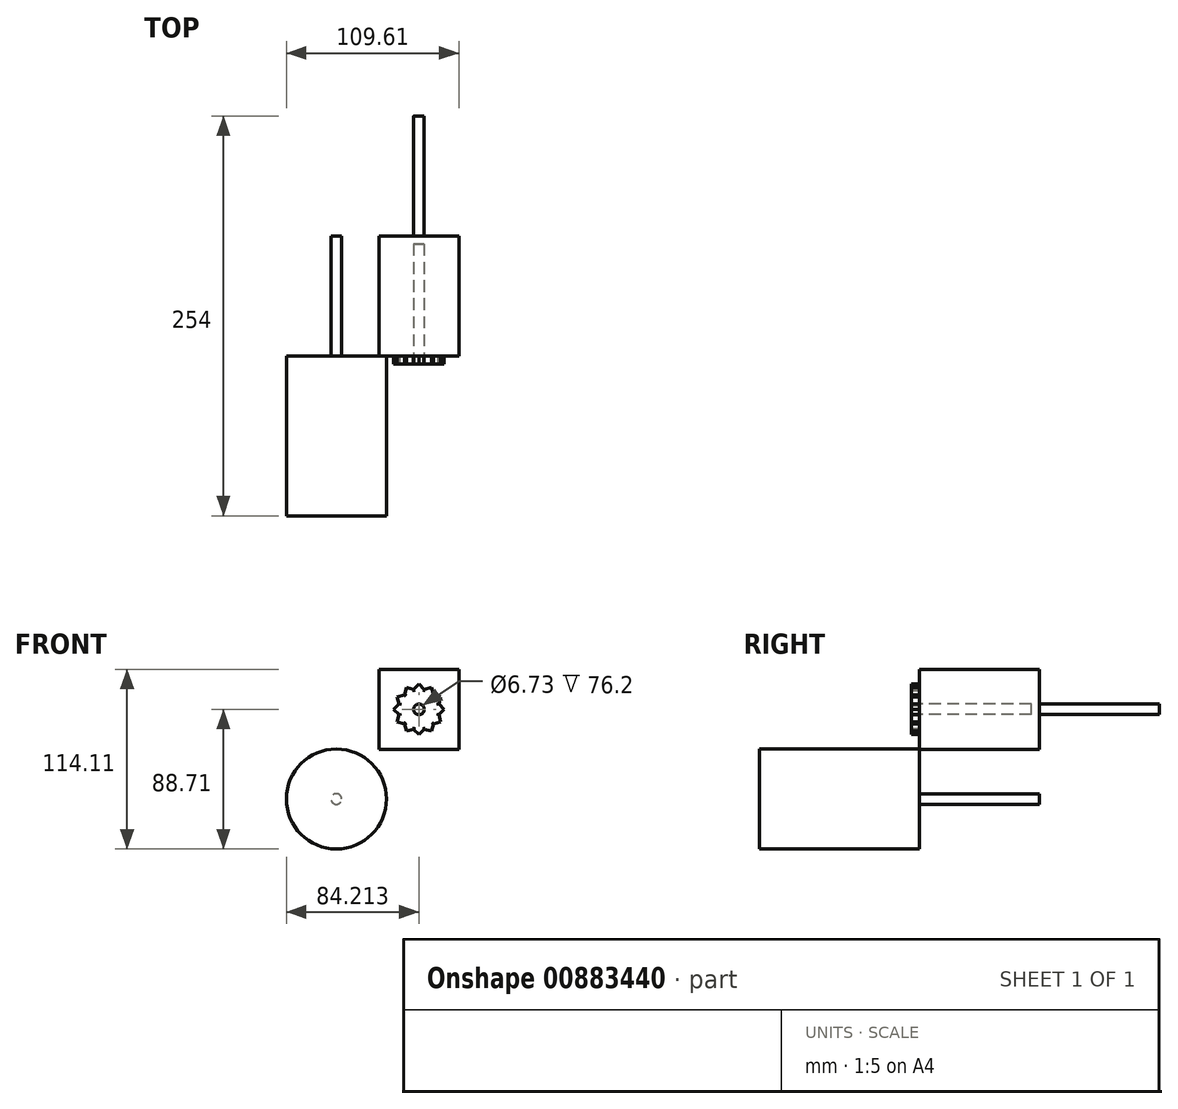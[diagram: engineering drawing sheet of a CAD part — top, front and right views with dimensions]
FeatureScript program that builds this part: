
annotation { "Feature Type Name" : "Feature", "Feature Type Description" : "" }
export const myFeature = defineFeature(function(context is Context, id is Id, definition is map)
    precondition{}
    {
        {
            var Q0;
            Q0=qCreatedBy(makeId("Front.planeOp"),FACE);
            var sketch = newSketch(context, id + "F0", { "sketchPlane" : qUnion([Q0])});
            skCircle(sketch, "E0", {"center": v(0, 0) * mm, "radius": 3.35 * mm});
            skSolve(sketch);
        }
        {
            var Q0;
            Q0 = qSketchRegion(id + "F0", true);
            extrude(context, id + "F1", {"entities" : qUnion([Q0]), "depth" : 76.2 * mm, "offsetDistance" : 25.4 * mm});
        }
        {
            var Q0;
            Q0=makeQuery(id+"F1.opExtrude","CAP_FACE",FACE,{"disambiguationData":[OSD([sQuery(id+"F0.wireOp",EDGE,"E0")])],"isStart":false});
            var sketch = newSketch(context, id + "F2", { "sketchPlane" : qUnion([Q0])});
            skCircle(sketch, "E1", {"center": v(0, 0) * mm, "radius": 31.75 * mm});
            skSolve(sketch);
        }
        {
            var Q0;
            Q0 = qSketchRegion(id + "F2", true);
            extrude(context, id + "F3", {"entities" : qUnion([Q0]), "operationType" : NewBodyOperationType.ADD, "depth" : 101.6 * mm, "offsetDistance" : 25.4 * mm});
        }
        {
            var Q0;
            Q0=qCreatedBy(makeId("Front.planeOp"),FACE);
            var sketch = newSketch(context, id + "F4", { "sketchPlane" : qUnion([Q0])});
            skLineSegment(sketch, "E2.bottom", {"start": v(27.06, 82.36) * mm, "end": v(77.86, 82.36) * mm});
            skLineSegment(sketch, "E2.top", {"start": v(27.06, 31.56) * mm, "end": v(77.86, 31.56) * mm});
            skLineSegment(sketch, "E2.left", {"start": v(27.06, 82.36) * mm, "end": v(27.06, 31.56) * mm});
            skLineSegment(sketch, "E2.right", {"start": v(77.86, 82.36) * mm, "end": v(77.86, 31.56) * mm});
            skSolve(sketch);
        }
        {
            var Q0;
            Q0 = qSketchRegion(id + "F4", true);
            extrude(context, id + "F5", {"entities" : qUnion([Q0]), "depth" : 76.2 * mm, "offsetDistance" : 25.4 * mm});
        }
        {
            var Q0;
            Q0=makeQuery(id+"F5.opExtrude","CAP_FACE",FACE,{"disambiguationData":[OSD([sQuery(id+"F4.wireOp",EDGE,"E2.bottom"),sQuery(id+"F4.wireOp",EDGE,"E2.top"),sQuery(id+"F4.wireOp",EDGE,"E2.left"),sQuery(id+"F4.wireOp",EDGE,"E2.right")])],"isStart":true});
            var sketch = newSketch(context, id + "F6", { "sketchPlane" : qUnion([Q0])});
            skCircle(sketch, "E3", {"center": v(-52.46, 56.96) * mm, "radius": 3.35 * mm});
            skSolve(sketch);
        }
        {
            var Q0;
            Q0 = qSketchRegion(id + "F6", true);
            extrude(context, id + "F7", {"entities" : qUnion([Q0]), "operationType" : NewBodyOperationType.ADD, "depth" : 76.2 * mm, "offsetDistance" : 25.4 * mm});
        }
        {
            var Q0;
            Q0=makeQuery(id+"F5.opExtrude","CAP_FACE",FACE,{"disambiguationData":[OSD([sQuery(id+"F4.wireOp",EDGE,"E2.bottom"),sQuery(id+"F4.wireOp",EDGE,"E2.top"),sQuery(id+"F4.wireOp",EDGE,"E2.left"),sQuery(id+"F4.wireOp",EDGE,"E2.right")])],"isStart":false});
            var sketch = newSketch(context, id + "F8", { "sketchPlane" : qUnion([Q0])});
            skCircle(sketch, "E4", {"center": v(52.46, 56.96) * mm, "radius": 12.7 * mm});
            skLineSegment(sketch, "E5", {"start": v(48.51, 69.03) * mm, "end": v(52.46, 72.98) * mm});
            skLineSegment(sketch, "E6", {"start": v(56.41, 69.03) * mm, "end": v(52.46, 72.98) * mm});
            skLineSegment(sketch, "E7", {"start": v(48.51, 69.03) * mm, "end": v(56.41, 69.03) * mm});
            skLineSegment(sketch, "E8.1.0", {"start": v(49.85, 69.39) * mm, "end": v(44.45, 70.83) * mm});
            skLineSegment(sketch, "E8.1.1", {"start": v(43, 65.44) * mm, "end": v(44.45, 70.83) * mm});
            skLineSegment(sketch, "E8.1.2", {"start": v(43, 65.44) * mm, "end": v(49.85, 69.39) * mm});
            skLineSegment(sketch, "E8.2.0", {"start": v(43.99, 66.42) * mm, "end": v(38.59, 64.97) * mm});
            skLineSegment(sketch, "E8.2.1", {"start": v(40.03, 59.57) * mm, "end": v(38.59, 64.97) * mm});
            skLineSegment(sketch, "E8.2.2", {"start": v(40.03, 59.57) * mm, "end": v(43.99, 66.42) * mm});
            skLineSegment(sketch, "E8.3.0", {"start": v(40.4, 60.91) * mm, "end": v(36.44, 56.96) * mm});
            skLineSegment(sketch, "E8.3.1", {"start": v(40.4, 53) * mm, "end": v(36.44, 56.96) * mm});
            skLineSegment(sketch, "E8.3.2", {"start": v(40.4, 53) * mm, "end": v(40.4, 60.91) * mm});
            skLineSegment(sketch, "E8.4.0", {"start": v(40.03, 54.35) * mm, "end": v(38.59, 48.95) * mm});
            skLineSegment(sketch, "E8.4.1", {"start": v(43.99, 47.5) * mm, "end": v(38.59, 48.95) * mm});
            skLineSegment(sketch, "E8.4.2", {"start": v(43.99, 47.5) * mm, "end": v(40.03, 54.35) * mm});
            skLineSegment(sketch, "E8.5.0", {"start": v(43, 48.48) * mm, "end": v(44.45, 43.09) * mm});
            skLineSegment(sketch, "E8.5.1", {"start": v(49.85, 44.53) * mm, "end": v(44.45, 43.09) * mm});
            skLineSegment(sketch, "E8.5.2", {"start": v(49.85, 44.53) * mm, "end": v(43, 48.48) * mm});
            skLineSegment(sketch, "E8.6.0", {"start": v(48.51, 44.89) * mm, "end": v(52.46, 40.94) * mm});
            skLineSegment(sketch, "E8.6.1", {"start": v(56.41, 44.89) * mm, "end": v(52.46, 40.94) * mm});
            skLineSegment(sketch, "E8.6.2", {"start": v(56.41, 44.89) * mm, "end": v(48.51, 44.89) * mm});
            skLineSegment(sketch, "E8.7.0", {"start": v(55.08, 44.53) * mm, "end": v(60.47, 43.09) * mm});
            skLineSegment(sketch, "E8.7.1", {"start": v(61.92, 48.48) * mm, "end": v(60.47, 43.09) * mm});
            skLineSegment(sketch, "E8.7.2", {"start": v(61.92, 48.48) * mm, "end": v(55.08, 44.53) * mm});
            skLineSegment(sketch, "E8.8.0", {"start": v(60.94, 47.5) * mm, "end": v(66.34, 48.95) * mm});
            skLineSegment(sketch, "E8.8.1", {"start": v(64.9, 54.35) * mm, "end": v(66.34, 48.95) * mm});
            skLineSegment(sketch, "E8.8.2", {"start": v(64.9, 54.35) * mm, "end": v(60.94, 47.5) * mm});
            skLineSegment(sketch, "E8.9.0", {"start": v(64.53, 53) * mm, "end": v(68.48, 56.96) * mm});
            skLineSegment(sketch, "E8.9.1", {"start": v(64.53, 60.91) * mm, "end": v(68.48, 56.96) * mm});
            skLineSegment(sketch, "E8.9.2", {"start": v(64.53, 60.91) * mm, "end": v(64.53, 53) * mm});
            skLineSegment(sketch, "E8.10.0", {"start": v(64.9, 59.57) * mm, "end": v(66.34, 64.97) * mm});
            skLineSegment(sketch, "E8.10.1", {"start": v(60.94, 66.42) * mm, "end": v(66.34, 64.97) * mm});
            skLineSegment(sketch, "E8.10.2", {"start": v(60.94, 66.42) * mm, "end": v(64.9, 59.57) * mm});
            skLineSegment(sketch, "E8.11.0", {"start": v(61.92, 65.44) * mm, "end": v(60.47, 70.83) * mm});
            skLineSegment(sketch, "E8.11.1", {"start": v(55.08, 69.39) * mm, "end": v(60.47, 70.83) * mm});
            skLineSegment(sketch, "E8.11.2", {"start": v(55.08, 69.39) * mm, "end": v(61.92, 65.44) * mm});
            skSolve(sketch);
        }
        {
            var Q0;
            {var subQ0=sQuery(id+"F8.wireOp",EDGE,"E8.9.1");var subQ3=sQuery(id+"F8.wireOp",EDGE,"E8.10.0");var subQ5=makeQuery(id+"F8.imprint","INTERSECT",VERTEX,{"derivedFrom":[subQ0,subQ3]});Q0=makeQuery(id+"F8.imprint","IMPRINT",FACE,{"disambiguationData":[TD([[makeQuery(id+"F8.imprint","IMPRINT",EDGE,{"disambiguationData":[TD([[subQ5,1.0]])],"derivedFrom":subQ0}),-1.0]])]});}
            var Q1;
            {var subQ0=sQuery(id+"F8.wireOp",EDGE,"E8.10.1");var subQ3=sQuery(id+"F8.wireOp",EDGE,"E8.11.0");var subQ5=makeQuery(id+"F8.imprint","INTERSECT",VERTEX,{"derivedFrom":[subQ0,subQ3]});Q1=makeQuery(id+"F8.imprint","IMPRINT",FACE,{"disambiguationData":[TD([[makeQuery(id+"F8.imprint","IMPRINT",EDGE,{"disambiguationData":[TD([[subQ5,1.0]])],"derivedFrom":subQ0}),-1.0]])]});}
            var Q2;
            {var subQ0=sQuery(id+"F8.wireOp",EDGE,"E6");var subQ3=sQuery(id+"F8.wireOp",EDGE,"E8.11.1");var subQ5=makeQuery(id+"F8.imprint","INTERSECT",VERTEX,{"derivedFrom":[subQ0,subQ3]});Q2=makeQuery(id+"F8.imprint","IMPRINT",FACE,{"disambiguationData":[TD([[makeQuery(id+"F8.imprint","IMPRINT",EDGE,{"disambiguationData":[TD([[subQ5,1.0]])],"derivedFrom":subQ0}),1.0]])]});}
            var Q3;
            {var subQ0=sQuery(id+"F8.wireOp",EDGE,"E5");var subQ3=sQuery(id+"F8.wireOp",EDGE,"E8.1.0");var subQ5=makeQuery(id+"F8.imprint","INTERSECT",VERTEX,{"derivedFrom":[subQ0,subQ3]});Q3=makeQuery(id+"F8.imprint","IMPRINT",FACE,{"disambiguationData":[TD([[makeQuery(id+"F8.imprint","IMPRINT",EDGE,{"disambiguationData":[TD([[subQ5,1.0]])],"derivedFrom":subQ0}),-1.0]])]});}
            var Q4;
            {var subQ0=sQuery(id+"F8.wireOp",EDGE,"E8.1.1");var subQ3=sQuery(id+"F8.wireOp",EDGE,"E8.2.0");var subQ5=makeQuery(id+"F8.imprint","INTERSECT",VERTEX,{"derivedFrom":[subQ0,subQ3]});Q4=makeQuery(id+"F8.imprint","IMPRINT",FACE,{"disambiguationData":[TD([[makeQuery(id+"F8.imprint","IMPRINT",EDGE,{"disambiguationData":[TD([[subQ5,1.0]])],"derivedFrom":subQ0}),-1.0]])]});}
            var Q5;
            {var subQ0=sQuery(id+"F8.wireOp",EDGE,"E8.2.1");var subQ3=sQuery(id+"F8.wireOp",EDGE,"E8.3.0");var subQ5=makeQuery(id+"F8.imprint","INTERSECT",VERTEX,{"derivedFrom":[subQ0,subQ3]});Q5=makeQuery(id+"F8.imprint","IMPRINT",FACE,{"disambiguationData":[TD([[makeQuery(id+"F8.imprint","IMPRINT",EDGE,{"disambiguationData":[TD([[subQ5,1.0]])],"derivedFrom":subQ0}),-1.0]])]});}
            var Q6;
            {var subQ0=sQuery(id+"F8.wireOp",EDGE,"E8.3.1");var subQ3=sQuery(id+"F8.wireOp",EDGE,"E8.4.0");var subQ5=makeQuery(id+"F8.imprint","INTERSECT",VERTEX,{"derivedFrom":[subQ0,subQ3]});Q6=makeQuery(id+"F8.imprint","IMPRINT",FACE,{"disambiguationData":[TD([[makeQuery(id+"F8.imprint","IMPRINT",EDGE,{"disambiguationData":[TD([[subQ5,1.0]])],"derivedFrom":subQ0}),-1.0]])]});}
            var Q7;
            {var subQ0=sQuery(id+"F8.wireOp",EDGE,"E8.4.1");var subQ3=sQuery(id+"F8.wireOp",EDGE,"E8.5.0");var subQ5=makeQuery(id+"F8.imprint","INTERSECT",VERTEX,{"derivedFrom":[subQ0,subQ3]});Q7=makeQuery(id+"F8.imprint","IMPRINT",FACE,{"disambiguationData":[TD([[makeQuery(id+"F8.imprint","IMPRINT",EDGE,{"disambiguationData":[TD([[subQ5,1.0]])],"derivedFrom":subQ0}),-1.0]])]});}
            var Q8;
            {var subQ0=sQuery(id+"F8.wireOp",EDGE,"E8.5.1");var subQ3=sQuery(id+"F8.wireOp",EDGE,"E8.6.0");var subQ5=makeQuery(id+"F8.imprint","INTERSECT",VERTEX,{"derivedFrom":[subQ0,subQ3]});Q8=makeQuery(id+"F8.imprint","IMPRINT",FACE,{"disambiguationData":[TD([[makeQuery(id+"F8.imprint","IMPRINT",EDGE,{"disambiguationData":[TD([[subQ5,1.0]])],"derivedFrom":subQ0}),-1.0]])]});}
            var Q9;
            {var subQ0=sQuery(id+"F8.wireOp",EDGE,"E8.6.1");var subQ3=sQuery(id+"F8.wireOp",EDGE,"E8.7.0");var subQ5=makeQuery(id+"F8.imprint","INTERSECT",VERTEX,{"derivedFrom":[subQ0,subQ3]});Q9=makeQuery(id+"F8.imprint","IMPRINT",FACE,{"disambiguationData":[TD([[makeQuery(id+"F8.imprint","IMPRINT",EDGE,{"disambiguationData":[TD([[subQ5,1.0]])],"derivedFrom":subQ0}),-1.0]])]});}
            var Q10;
            {var subQ0=sQuery(id+"F8.wireOp",EDGE,"E8.7.1");var subQ3=sQuery(id+"F8.wireOp",EDGE,"E8.8.0");var subQ5=makeQuery(id+"F8.imprint","INTERSECT",VERTEX,{"derivedFrom":[subQ0,subQ3]});Q10=makeQuery(id+"F8.imprint","IMPRINT",FACE,{"disambiguationData":[TD([[makeQuery(id+"F8.imprint","IMPRINT",EDGE,{"disambiguationData":[TD([[subQ5,1.0]])],"derivedFrom":subQ0}),-1.0]])]});}
            var Q11;
            {var subQ0=sQuery(id+"F8.wireOp",EDGE,"E8.8.1");var subQ3=sQuery(id+"F8.wireOp",EDGE,"E8.9.0");var subQ5=makeQuery(id+"F8.imprint","INTERSECT",VERTEX,{"derivedFrom":[subQ0,subQ3]});Q11=makeQuery(id+"F8.imprint","IMPRINT",FACE,{"disambiguationData":[TD([[makeQuery(id+"F8.imprint","IMPRINT",EDGE,{"disambiguationData":[TD([[subQ5,1.0]])],"derivedFrom":subQ0}),-1.0]])]});}
            var Q12;
            {var subQ0=sQuery(id+"F8.wireOp",EDGE,"E8.10.1");var subQ1=sQuery(id+"F8.wireOp",EDGE,"E8.10.0");var subQ2=makeQuery(id+"F8.imprint","INTERSECT",VERTEX,{"derivedFrom":[subQ1,subQ0]});Q12=makeQuery(id+"F8.imprint","IMPRINT",FACE,{"disambiguationData":[TD([[makeQuery(id+"F8.imprint","IMPRINT",EDGE,{"disambiguationData":[TD([[subQ2,1.0]])],"derivedFrom":subQ1}),1.0]])]});}
            var Q13;
            {var subQ0=sQuery(id+"F8.wireOp",EDGE,"E8.11.1");var subQ1=sQuery(id+"F8.wireOp",EDGE,"E8.11.0");var subQ2=makeQuery(id+"F8.imprint","INTERSECT",VERTEX,{"derivedFrom":[subQ1,subQ0]});Q13=makeQuery(id+"F8.imprint","IMPRINT",FACE,{"disambiguationData":[TD([[makeQuery(id+"F8.imprint","IMPRINT",EDGE,{"disambiguationData":[TD([[subQ2,1.0]])],"derivedFrom":subQ1}),1.0]])]});}
            var Q14;
            {var subQ3=sQuery(id+"F8.wireOp",EDGE,"E5");var subQ5=sQuery(id+"F8.wireOp",EDGE,"E6");var subQ6=makeQuery(id+"F8.imprint","INTERSECT",VERTEX,{"derivedFrom":[subQ3,subQ5]});Q14=makeQuery(id+"F8.imprint","IMPRINT",FACE,{"disambiguationData":[TD([[makeQuery(id+"F8.imprint","IMPRINT",EDGE,{"disambiguationData":[TD([[subQ6,1.0]])],"derivedFrom":subQ3}),-1.0]])]});}
            var Q15;
            {var subQ0=sQuery(id+"F8.wireOp",EDGE,"E8.2.1");var subQ1=sQuery(id+"F8.wireOp",EDGE,"E8.2.0");var subQ2=makeQuery(id+"F8.imprint","INTERSECT",VERTEX,{"derivedFrom":[subQ1,subQ0]});Q15=makeQuery(id+"F8.imprint","IMPRINT",FACE,{"disambiguationData":[TD([[makeQuery(id+"F8.imprint","IMPRINT",EDGE,{"disambiguationData":[TD([[subQ2,1.0]])],"derivedFrom":subQ1}),1.0]])]});}
            var Q16;
            {var subQ0=sQuery(id+"F8.wireOp",EDGE,"E8.3.1");var subQ1=sQuery(id+"F8.wireOp",EDGE,"E8.3.0");var subQ2=makeQuery(id+"F8.imprint","INTERSECT",VERTEX,{"derivedFrom":[subQ1,subQ0]});Q16=makeQuery(id+"F8.imprint","IMPRINT",FACE,{"disambiguationData":[TD([[makeQuery(id+"F8.imprint","IMPRINT",EDGE,{"disambiguationData":[TD([[subQ2,1.0]])],"derivedFrom":subQ1}),1.0]])]});}
            var Q17;
            {var subQ0=sQuery(id+"F8.wireOp",EDGE,"E8.4.1");var subQ1=sQuery(id+"F8.wireOp",EDGE,"E8.4.0");var subQ2=makeQuery(id+"F8.imprint","INTERSECT",VERTEX,{"derivedFrom":[subQ1,subQ0]});Q17=makeQuery(id+"F8.imprint","IMPRINT",FACE,{"disambiguationData":[TD([[makeQuery(id+"F8.imprint","IMPRINT",EDGE,{"disambiguationData":[TD([[subQ2,1.0]])],"derivedFrom":subQ1}),1.0]])]});}
            var Q18;
            {var subQ0=sQuery(id+"F8.wireOp",EDGE,"E8.5.1");var subQ1=sQuery(id+"F8.wireOp",EDGE,"E8.5.0");var subQ2=makeQuery(id+"F8.imprint","INTERSECT",VERTEX,{"derivedFrom":[subQ1,subQ0]});Q18=makeQuery(id+"F8.imprint","IMPRINT",FACE,{"disambiguationData":[TD([[makeQuery(id+"F8.imprint","IMPRINT",EDGE,{"disambiguationData":[TD([[subQ2,1.0]])],"derivedFrom":subQ1}),1.0]])]});}
            var Q19;
            {var subQ0=sQuery(id+"F8.wireOp",EDGE,"E8.6.1");var subQ1=sQuery(id+"F8.wireOp",EDGE,"E8.6.0");var subQ2=makeQuery(id+"F8.imprint","INTERSECT",VERTEX,{"derivedFrom":[subQ1,subQ0]});Q19=makeQuery(id+"F8.imprint","IMPRINT",FACE,{"disambiguationData":[TD([[makeQuery(id+"F8.imprint","IMPRINT",EDGE,{"disambiguationData":[TD([[subQ2,1.0]])],"derivedFrom":subQ1}),1.0]])]});}
            var Q20;
            {var subQ0=sQuery(id+"F8.wireOp",EDGE,"E8.7.1");var subQ1=sQuery(id+"F8.wireOp",EDGE,"E8.7.0");var subQ2=makeQuery(id+"F8.imprint","INTERSECT",VERTEX,{"derivedFrom":[subQ1,subQ0]});Q20=makeQuery(id+"F8.imprint","IMPRINT",FACE,{"disambiguationData":[TD([[makeQuery(id+"F8.imprint","IMPRINT",EDGE,{"disambiguationData":[TD([[subQ2,1.0]])],"derivedFrom":subQ1}),1.0]])]});}
            var Q21;
            {var subQ0=sQuery(id+"F8.wireOp",EDGE,"E8.8.1");var subQ1=sQuery(id+"F8.wireOp",EDGE,"E8.8.0");var subQ2=makeQuery(id+"F8.imprint","INTERSECT",VERTEX,{"derivedFrom":[subQ1,subQ0]});Q21=makeQuery(id+"F8.imprint","IMPRINT",FACE,{"disambiguationData":[TD([[makeQuery(id+"F8.imprint","IMPRINT",EDGE,{"disambiguationData":[TD([[subQ2,1.0]])],"derivedFrom":subQ1}),1.0]])]});}
            var Q22;
            {var subQ0=sQuery(id+"F8.wireOp",EDGE,"E8.9.1");var subQ1=sQuery(id+"F8.wireOp",EDGE,"E8.9.0");var subQ2=makeQuery(id+"F8.imprint","INTERSECT",VERTEX,{"derivedFrom":[subQ1,subQ0]});Q22=makeQuery(id+"F8.imprint","IMPRINT",FACE,{"disambiguationData":[TD([[makeQuery(id+"F8.imprint","IMPRINT",EDGE,{"disambiguationData":[TD([[subQ2,1.0]])],"derivedFrom":subQ1}),1.0]])]});}
            var Q23;
            {var subQ15=sQuery(id+"F8.wireOp",EDGE,"E8.1.2");var subQ16=sQuery(id+"F8.wireOp",EDGE,"E7");var subQ17=makeQuery(id+"F8.imprint","INTERSECT",VERTEX,{"derivedFrom":[subQ16,subQ15]});Q23=makeQuery(id+"F8.imprint","IMPRINT",FACE,{"disambiguationData":[TD([[makeQuery(id+"F8.imprint","IMPRINT",EDGE,{"disambiguationData":[TD([[subQ17,-1.0]])],"derivedFrom":subQ16}),-1.0]])]});}
            var Q24;
            {var subQ0=sQuery(id+"F8.wireOp",EDGE,"E7");var subQ5=sQuery(id+"F8.wireOp",EDGE,"E8.1.2");var subQ6=makeQuery(id+"F8.imprint","INTERSECT",VERTEX,{"derivedFrom":[subQ0,subQ5]});Q24=makeQuery(id+"F8.imprint","IMPRINT",FACE,{"disambiguationData":[TD([[makeQuery(id+"F8.imprint","IMPRINT",EDGE,{"disambiguationData":[TD([[subQ6,1.0]])],"derivedFrom":subQ5}),1.0]])]});}
            var Q25;
            {var subQ0=sQuery(id+"F8.wireOp",EDGE,"E8.1.1");var subQ1=sQuery(id+"F8.wireOp",EDGE,"E8.1.0");var subQ2=makeQuery(id+"F8.imprint","INTERSECT",VERTEX,{"derivedFrom":[subQ1,subQ0]});Q25=makeQuery(id+"F8.imprint","IMPRINT",FACE,{"disambiguationData":[TD([[makeQuery(id+"F8.imprint","IMPRINT",EDGE,{"disambiguationData":[TD([[subQ2,1.0]])],"derivedFrom":subQ1}),1.0]])]});}
            var Q26;
            {var subQ0=sQuery(id+"F8.wireOp",EDGE,"E8.1.2");var subQ5=sQuery(id+"F8.wireOp",EDGE,"E7");var subQ7=makeQuery(id+"F8.imprint","INTERSECT",VERTEX,{"derivedFrom":[subQ5,subQ0]});Q26=makeQuery(id+"F8.imprint","IMPRINT",FACE,{"disambiguationData":[TD([[makeQuery(id+"F8.imprint","IMPRINT",EDGE,{"disambiguationData":[TD([[subQ7,-1.0]])],"derivedFrom":subQ5}),1.0]])]});}
            var Q27;
            {var subQ0=sQuery(id+"F8.wireOp",EDGE,"E7");var subQ5=sQuery(id+"F8.wireOp",EDGE,"E8.11.2");var subQ7=makeQuery(id+"F8.imprint","INTERSECT",VERTEX,{"derivedFrom":[subQ0,subQ5]});Q27=makeQuery(id+"F8.imprint","IMPRINT",FACE,{"disambiguationData":[TD([[makeQuery(id+"F8.imprint","IMPRINT",EDGE,{"disambiguationData":[TD([[subQ7,-1.0]])],"derivedFrom":subQ5}),1.0]])]});}
            var Q28;
            {var subQ0=sQuery(id+"F8.wireOp",EDGE,"E8.9.2");var subQ5=sQuery(id+"F8.wireOp",EDGE,"E8.10.2");var subQ6=makeQuery(id+"F8.imprint","INTERSECT",VERTEX,{"derivedFrom":[subQ0,subQ5]});Q28=makeQuery(id+"F8.imprint","IMPRINT",FACE,{"disambiguationData":[TD([[makeQuery(id+"F8.imprint","IMPRINT",EDGE,{"disambiguationData":[TD([[subQ6,1.0]])],"derivedFrom":subQ5}),1.0]])]});}
            var Q29;
            {var subQ0=sQuery(id+"F8.wireOp",EDGE,"E8.8.2");var subQ5=sQuery(id+"F8.wireOp",EDGE,"E8.9.2");var subQ6=makeQuery(id+"F8.imprint","INTERSECT",VERTEX,{"derivedFrom":[subQ0,subQ5]});Q29=makeQuery(id+"F8.imprint","IMPRINT",FACE,{"disambiguationData":[TD([[makeQuery(id+"F8.imprint","IMPRINT",EDGE,{"disambiguationData":[TD([[subQ6,1.0]])],"derivedFrom":subQ5}),1.0]])]});}
            var Q30;
            {var subQ0=sQuery(id+"F8.wireOp",EDGE,"E8.7.2");var subQ5=sQuery(id+"F8.wireOp",EDGE,"E8.8.2");var subQ6=makeQuery(id+"F8.imprint","INTERSECT",VERTEX,{"derivedFrom":[subQ0,subQ5]});Q30=makeQuery(id+"F8.imprint","IMPRINT",FACE,{"disambiguationData":[TD([[makeQuery(id+"F8.imprint","IMPRINT",EDGE,{"disambiguationData":[TD([[subQ6,1.0]])],"derivedFrom":subQ5}),1.0]])]});}
            var Q31;
            {var subQ0=sQuery(id+"F8.wireOp",EDGE,"E8.6.2");var subQ5=sQuery(id+"F8.wireOp",EDGE,"E8.7.2");var subQ6=makeQuery(id+"F8.imprint","INTERSECT",VERTEX,{"derivedFrom":[subQ0,subQ5]});Q31=makeQuery(id+"F8.imprint","IMPRINT",FACE,{"disambiguationData":[TD([[makeQuery(id+"F8.imprint","IMPRINT",EDGE,{"disambiguationData":[TD([[subQ6,1.0]])],"derivedFrom":subQ5}),1.0]])]});}
            var Q32;
            {var subQ0=sQuery(id+"F8.wireOp",EDGE,"E8.5.2");var subQ5=sQuery(id+"F8.wireOp",EDGE,"E8.6.2");var subQ6=makeQuery(id+"F8.imprint","INTERSECT",VERTEX,{"derivedFrom":[subQ0,subQ5]});Q32=makeQuery(id+"F8.imprint","IMPRINT",FACE,{"disambiguationData":[TD([[makeQuery(id+"F8.imprint","IMPRINT",EDGE,{"disambiguationData":[TD([[subQ6,1.0]])],"derivedFrom":subQ5}),1.0]])]});}
            var Q33;
            {var subQ0=sQuery(id+"F8.wireOp",EDGE,"E8.4.2");var subQ5=sQuery(id+"F8.wireOp",EDGE,"E8.5.2");var subQ6=makeQuery(id+"F8.imprint","INTERSECT",VERTEX,{"derivedFrom":[subQ0,subQ5]});Q33=makeQuery(id+"F8.imprint","IMPRINT",FACE,{"disambiguationData":[TD([[makeQuery(id+"F8.imprint","IMPRINT",EDGE,{"disambiguationData":[TD([[subQ6,1.0]])],"derivedFrom":subQ5}),1.0]])]});}
            var Q34;
            {var subQ0=sQuery(id+"F8.wireOp",EDGE,"E8.3.2");var subQ5=sQuery(id+"F8.wireOp",EDGE,"E8.4.2");var subQ6=makeQuery(id+"F8.imprint","INTERSECT",VERTEX,{"derivedFrom":[subQ0,subQ5]});Q34=makeQuery(id+"F8.imprint","IMPRINT",FACE,{"disambiguationData":[TD([[makeQuery(id+"F8.imprint","IMPRINT",EDGE,{"disambiguationData":[TD([[subQ6,1.0]])],"derivedFrom":subQ5}),1.0]])]});}
            var Q35;
            {var subQ0=sQuery(id+"F8.wireOp",EDGE,"E8.2.2");var subQ5=sQuery(id+"F8.wireOp",EDGE,"E8.3.2");var subQ6=makeQuery(id+"F8.imprint","INTERSECT",VERTEX,{"derivedFrom":[subQ0,subQ5]});Q35=makeQuery(id+"F8.imprint","IMPRINT",FACE,{"disambiguationData":[TD([[makeQuery(id+"F8.imprint","IMPRINT",EDGE,{"disambiguationData":[TD([[subQ6,1.0]])],"derivedFrom":subQ5}),1.0]])]});}
            var Q36;
            {var subQ0=sQuery(id+"F8.wireOp",EDGE,"E8.1.2");var subQ5=sQuery(id+"F8.wireOp",EDGE,"E8.2.2");var subQ6=makeQuery(id+"F8.imprint","INTERSECT",VERTEX,{"derivedFrom":[subQ0,subQ5]});Q36=makeQuery(id+"F8.imprint","IMPRINT",FACE,{"disambiguationData":[TD([[makeQuery(id+"F8.imprint","IMPRINT",EDGE,{"disambiguationData":[TD([[subQ6,1.0]])],"derivedFrom":subQ5}),1.0]])]});}
            extrude(context, id + "F9", {"entities" : qUnion([Q0, Q1, Q2, Q3, Q4, Q5, Q6, Q7, Q8, Q9, Q10, Q11, Q12, Q13, Q14, Q15, Q16, Q17, Q18, Q19, Q20, Q21, Q22, Q23, Q24, Q25, Q26, Q27, Q28, Q29, Q30, Q31, Q32, Q33, Q34, Q35, Q36]), "operationType" : NewBodyOperationType.ADD, "depth" : 5.08 * mm, "offsetDistance" : 25.4 * mm});
        }
        {
            var Q0;
            Q0=makeQuery(id+"F9.opExtrude","CAP_FACE",FACE,{"disambiguationData":[OSD([sQuery(id+"F8.wireOp",EDGE,"E4"),sQuery(id+"F8.wireOp",EDGE,"E5"),sQuery(id+"F8.wireOp",EDGE,"E6"),sQuery(id+"F8.wireOp",EDGE,"E7"),sQuery(id+"F8.wireOp",EDGE,"E8.1.0"),sQuery(id+"F8.wireOp",EDGE,"E8.1.1"),sQuery(id+"F8.wireOp",EDGE,"E8.1.2"),sQuery(id+"F8.wireOp",EDGE,"E8.2.0"),sQuery(id+"F8.wireOp",EDGE,"E8.2.1"),sQuery(id+"F8.wireOp",EDGE,"E8.2.2"),sQuery(id+"F8.wireOp",EDGE,"E8.3.0"),sQuery(id+"F8.wireOp",EDGE,"E8.3.1"),sQuery(id+"F8.wireOp",EDGE,"E8.3.2"),sQuery(id+"F8.wireOp",EDGE,"E8.4.0"),sQuery(id+"F8.wireOp",EDGE,"E8.4.1"),sQuery(id+"F8.wireOp",EDGE,"E8.4.2"),sQuery(id+"F8.wireOp",EDGE,"E8.5.0"),sQuery(id+"F8.wireOp",EDGE,"E8.5.1"),sQuery(id+"F8.wireOp",EDGE,"E8.5.2"),sQuery(id+"F8.wireOp",EDGE,"E8.6.0"),sQuery(id+"F8.wireOp",EDGE,"E8.6.1"),sQuery(id+"F8.wireOp",EDGE,"E8.6.2"),sQuery(id+"F8.wireOp",EDGE,"E8.7.0"),sQuery(id+"F8.wireOp",EDGE,"E8.7.1"),sQuery(id+"F8.wireOp",EDGE,"E8.7.2"),sQuery(id+"F8.wireOp",EDGE,"E8.8.0"),sQuery(id+"F8.wireOp",EDGE,"E8.8.1"),sQuery(id+"F8.wireOp",EDGE,"E8.8.2"),sQuery(id+"F8.wireOp",EDGE,"E8.9.0"),sQuery(id+"F8.wireOp",EDGE,"E8.9.1"),sQuery(id+"F8.wireOp",EDGE,"E8.9.2"),sQuery(id+"F8.wireOp",EDGE,"E8.10.0"),sQuery(id+"F8.wireOp",EDGE,"E8.10.1"),sQuery(id+"F8.wireOp",EDGE,"E8.10.2"),sQuery(id+"F8.wireOp",EDGE,"E8.11.0"),sQuery(id+"F8.wireOp",EDGE,"E8.11.1"),sQuery(id+"F8.wireOp",EDGE,"E8.11.2")])],"isStart":false});
            var sketch = newSketch(context, id + "F10", { "sketchPlane" : qUnion([Q0])});
            skCircle(sketch, "E9", {"center": v(52.46, 56.96) * mm, "radius": 3.37 * mm});
            skSolve(sketch);
        }
        {
            var Q0;
            Q0 = qSketchRegion(id + "F10", true);
            extrude(context, id + "F11", {"entities" : qUnion([Q0]), "operationType" : NewBodyOperationType.REMOVE, "oppositeDirection" : true, "depth" : 76.2 * mm, "offsetDistance" : 25.4 * mm});
        }
    });
